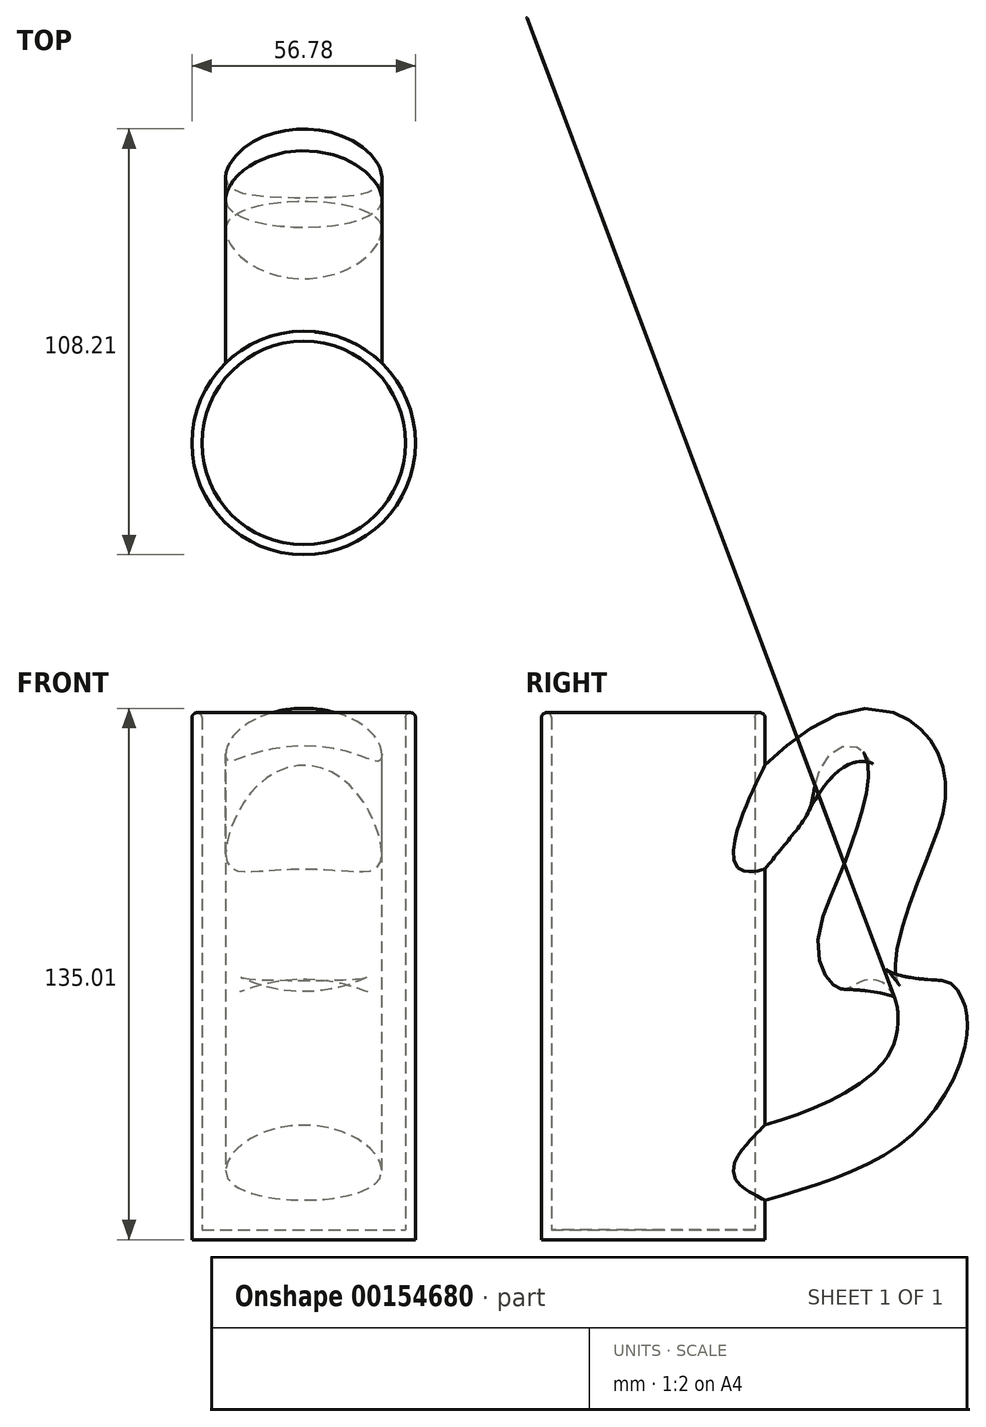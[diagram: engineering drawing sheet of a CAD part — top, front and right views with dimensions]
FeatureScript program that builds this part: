
annotation { "Feature Type Name" : "Feature", "Feature Type Description" : "" }
export const myFeature = defineFeature(function(context is Context, id is Id, definition is map)
    precondition{}
    {
        {
            var Q0;
            Q0=qCreatedBy(makeId("Front.planeOp"),FACE);
            var sketch = newSketch(context, id + "F0", { "sketchPlane" : qUnion([Q0])});
            skEllipse(sketch, "E0", {"center": v(0, 0) * mm, "majorRadius": 14.85 * mm, "minorRadius": 19.82 * mm, "majorAxis": v(0, 1)});
            skSolve(sketch);
        }
        {
            var Q0;
            Q0=qCreatedBy(makeId("Right.planeOp"),FACE);
            var sketch = newSketch(context, id + "F1", { "sketchPlane" : qUnion([Q0])});
            skFitSpline(sketch, "E1", {"points": [v(0, 0) * mm, v(50.4, 50.82) * mm, v(61.94, 42.06) * mm, v(54.56, 0) * mm, v(65.9, -12.39) * mm, v(60.47, -35.64) * mm, v(0, -59.7) * mm], "startDerivative": vector(236.23, 307.4) * mm, "endDerivative": vector(-327.32, -77) * mm});
            skSolve(sketch);
        }
        {
            var Q0;
            Q0=makeQuery(id+"F0.imprint","IMPRINT",FACE,{"disambiguationData":[TD([[makeQuery(id+"F0.imprint","IMPRINT",EDGE,{"derivedFrom":sQuery(id+"F0.wireOp",EDGE,"E0")}),1.0]])]});
            var Q1;
            Q1=sQuery(id+"F1.wireOp",EDGE,"E1");
            sweep(context, id + "F2", {"profiles" : qUnion([Q0]), "path" : qUnion([Q1])});
        }
        {
            var Q0;
            Q0=makeQuery(id+"F2.opSweep","CAP_FACE",FACE,{"disambiguationData":[OSD([sQuery(id+"F0.wireOp",EDGE,"E0"),sQuery(id+"F1.wireOp",VERTEX,"E1.start")])],"isStart":true});
            var sketch = newSketch(context, id + "F3", { "sketchPlane" : qUnion([Q0])});
            skCircle(sketch, "E2", {"center": v(0, 0) * mm, "radius": 13.33 * mm});
            skSolve(sketch);
        }
        {
            var Q0;
            Q0=qCreatedBy(makeId("Right.planeOp"),FACE);
            var sketch = newSketch(context, id + "F4", { "sketchPlane" : qUnion([Q0])});
            skFitSpline(sketch, "E3", {"points": [v(0, 0) * mm, v(-20.7, 12.72) * mm, v(-40.81, 27.74) * mm, v(-52.94, 38.92) * mm, v(-69.99, 65.44) * mm], "startDerivative": vector(-81.75, 47.42) * mm, "endDerivative": vector(-61.28, 104.97) * mm});
            skSolve(sketch);
        }
        {
            var Q0;
            Q0=qCreatedBy(makeId("Right.planeOp"),FACE);
            var sketch = newSketch(context, id + "F5", { "sketchPlane" : qUnion([Q0])});
            skLineSegment(sketch, "E4", {"start": v(0, -72.32) * mm, "end": v(0, 61.57) * mm});
            skLineSegment(sketch, "E5", {"start": v(0, 61.57) * mm, "end": v(28.4, 61.57) * mm});
            skLineSegment(sketch, "E6", {"start": v(28.4, -72.32) * mm, "end": v(28.4, 61.57) * mm});
            skLineSegment(sketch, "E7", {"start": v(0, -72.32) * mm, "end": v(28.4, -72.32) * mm});
            skSolve(sketch);
        }
        {
            var Q0;
            Q0 = qSketchRegion(id + "F5", true);
            var Q1;
            Q1=sQuery(id+"F5.wireOp",EDGE,"E4");
            revolve(context, id + "F6", {"operationType" : NewBodyOperationType.ADD, "entities" : qUnion([Q0]), "axis" : qUnion([Q1]), "revolveType" : RevolveType.FULL});
        }
        {
            var Q0;
            Q0=makeQuery(id+"F6.opRevolve","SWEPT_FACE",FACE,{"disambiguationData":[OSD([sQuery(id+"F5.wireOp",EDGE,"E5")])]});
            shell(context, id + "F7", {"entities" : qUnion([Q0]), "thickness" : 2.54 * mm});
        }
        {
            var Q0;
            Q0=makeQuery(id+"F6.opRevolve","SWEPT_FACE",FACE,{"disambiguationData":[OSD([sQuery(id+"F5.wireOp",EDGE,"E5")])]});
            fillet(context, id + "F8", {"entities" : qUnion([Q0]), "radius" : 1.27 * mm, "tangentPropagation" : true, "allowEdgeOverflow" : false});
        }
    });
